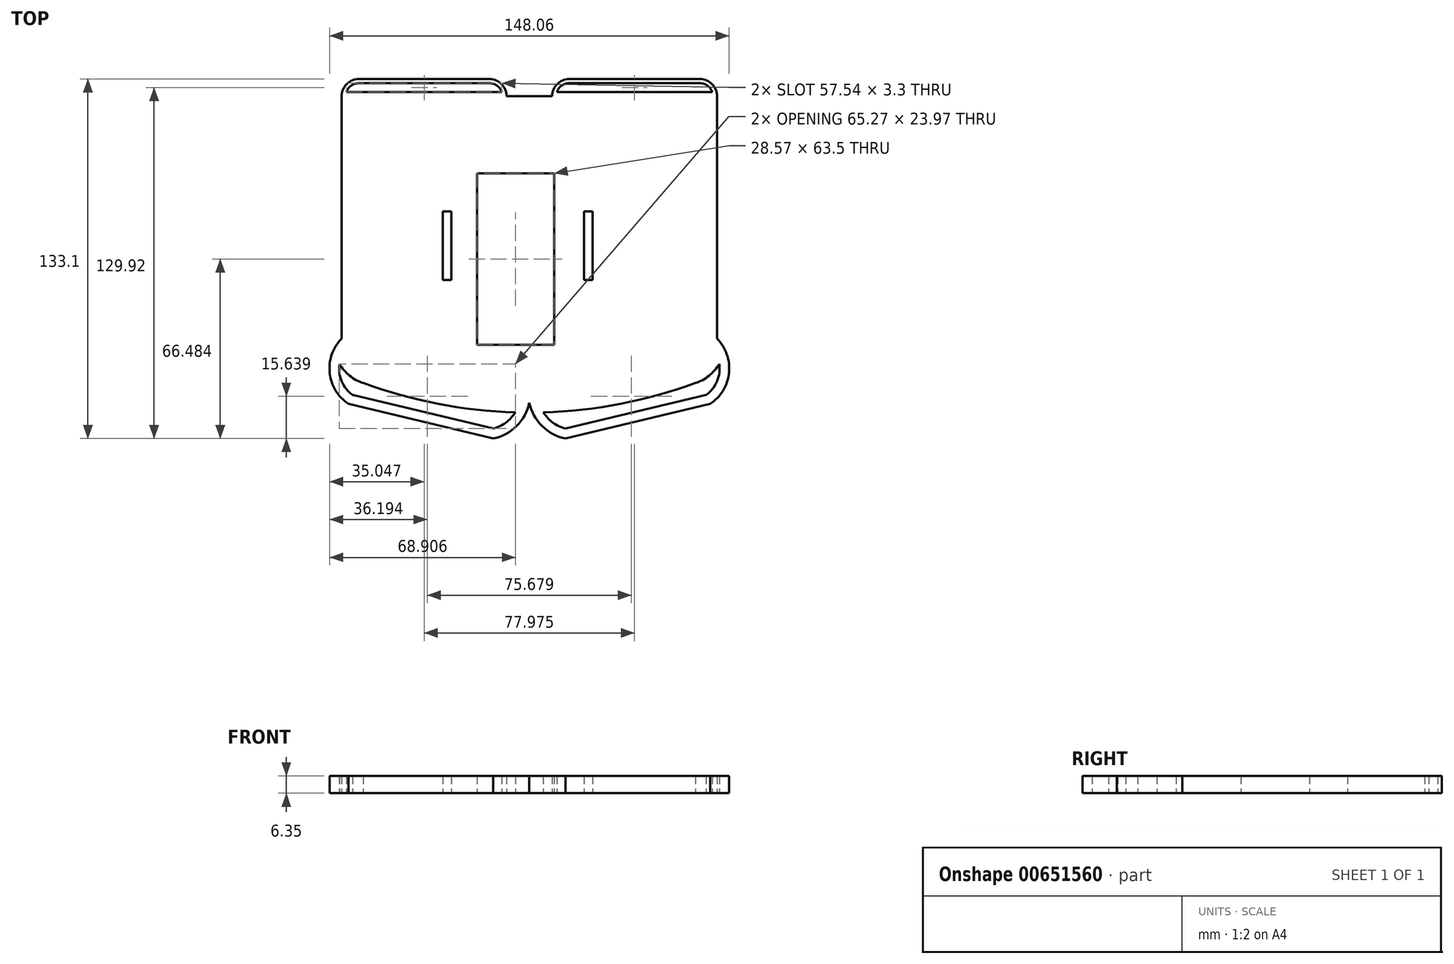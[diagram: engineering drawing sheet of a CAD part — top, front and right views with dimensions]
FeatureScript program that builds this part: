
annotation { "Feature Type Name" : "Feature", "Feature Type Description" : "" }
export const myFeature = defineFeature(function(context is Context, id is Id, definition is map)
    precondition{}
    {
        {
            var Q0;
            Q0=qCreatedBy(makeId("Top.planeOp"),FACE);
            var sketch = newSketch(context, id + "F0", { "sketchPlane" : qUnion([Q0])});
            skLineSegment(sketch, "E0", {"start": v(-4.1, 53.24) * mm, "end": v(12.8, 53.24) * mm});
            skPoint(sketch, "E1", {"position": v(4.35, -60.35) * mm});
            skLineSegment(sketch, "E2", {"start": v(-65.17, 41.8) * mm, "end": v(-65.17, -36.5) * mm});
            skLineSegment(sketch, "E3.MirrorCS", {"start": v(73.88, 41.8) * mm, "end": v(73.88, -36.5) * mm});
            skPoint(sketch, "E4.orphan", {"position": v(-65.17, -52.82) * mm});
            skPoint(sketch, "E5.orphan", {"position": v(73.88, -52.82) * mm});
            skPoint(sketch, "E6.visualSharp", {"position": v(-65.17, 53.24) * mm});
            skPoint(sketch, "E7.visualSharp", {"position": v(73.88, 53.24) * mm});
            skPoint(sketch, "E8.visualSharp", {"position": v(-65.17, -45.96) * mm});
            skPoint(sketch, "E9.visualSharp", {"position": v(73.88, -45.96) * mm});
            skLineSegment(sketch, "E10.top", {"start": v(-58.82, 59.59) * mm, "end": v(-10.44, 59.59) * mm});
            skLineSegment(sketch, "E10.left", {"start": v(-65.17, 41.8) * mm, "end": v(-65.17, 53.24) * mm});
            skLineSegment(sketch, "E11", {"start": v(-4.1, 53.24) * mm, "end": v(-4.1, 53.24) * mm});
            skPoint(sketch, "E12.orphan", {"position": v(4.35, 59.59) * mm});
            skPoint(sketch, "E13.visualSharp", {"position": v(-65.17, 59.59) * mm});
            skArc(sketch, "E13.filletArc", {"start": v(-58.82, 59.59) * mm, "mid": v(-63.31, 57.73) * mm, "end": v(-65.17, 53.24) * mm});
            skPoint(sketch, "E14.visualSharp", {"position": v(-4.1, 59.59) * mm});
            skArc(sketch, "E14.filletArc", {"start": v(-4.1, 53.24) * mm, "mid": v(-5.95, 57.73) * mm, "end": v(-10.44, 59.59) * mm});
            skArc(sketch, "E15.0", {"start": v(-58.82, 58.06) * mm, "mid": v(-61.65, 57.15) * mm, "end": v(-63.4, 54.76) * mm});
            skLineSegment(sketch, "E15.1", {"start": v(-58.82, 58.06) * mm, "end": v(-10.44, 58.06) * mm});
            skArc(sketch, "E15.2", {"start": v(-5.86, 54.76) * mm, "mid": v(-7.62, 57.15) * mm, "end": v(-10.44, 58.06) * mm});
            skLineSegment(sketch, "E15.3", {"start": v(-63.4, 54.76) * mm, "end": v(-5.86, 54.76) * mm});
            skArc(sketch, "E16.MirrorCS", {"start": v(12.8, 53.24) * mm, "mid": v(14.66, 57.73) * mm, "end": v(19.15, 59.59) * mm});
            skLineSegment(sketch, "E17.MirrorCS", {"start": v(67.53, 59.59) * mm, "end": v(19.15, 59.59) * mm});
            skArc(sketch, "E18.MirrorCS", {"start": v(14.57, 54.76) * mm, "mid": v(16.33, 57.15) * mm, "end": v(19.15, 58.06) * mm});
            skLineSegment(sketch, "E19.MirrorCS", {"start": v(67.53, 58.06) * mm, "end": v(19.15, 58.06) * mm});
            skLineSegment(sketch, "E20.MirrorCS", {"start": v(72.1, 54.76) * mm, "end": v(14.57, 54.76) * mm});
            skArc(sketch, "E21.MirrorCS", {"start": v(67.53, 59.59) * mm, "mid": v(72.02, 57.73) * mm, "end": v(73.88, 53.24) * mm});
            skArc(sketch, "E22.MirrorCS", {"start": v(67.53, 58.06) * mm, "mid": v(70.35, 57.15) * mm, "end": v(72.1, 54.76) * mm});
            skLineSegment(sketch, "E23", {"start": v(73.88, 41.8) * mm, "end": v(73.88, 53.24) * mm});
            skPoint(sketch, "E24.endSnap0", {"position": v(-62.66, -44.5) * mm});
            skLineSegment(sketch, "E25", {"start": v(-62.66, -60.72) * mm, "end": v(-8.99, -73.51) * mm});
            skArc(sketch, "E26", {"start": v(-65.17, -36.5) * mm, "mid": v(-69.6, -49.2) * mm, "end": v(-62.66, -60.72) * mm});
            skArc(sketch, "E27", {"start": v(-8.99, -73.51) * mm, "mid": v(-0.38, -68.9) * mm, "end": v(4.35, -60.35) * mm});
            skLineSegment(sketch, "E28.0", {"start": v(-66, -45.88) * mm, "end": v(-66, -45.88) * mm});
            skLineSegment(sketch, "E28.1", {"start": v(-61.17, -57.42) * mm, "end": v(-8.98, -69.86) * mm});
            skArc(sketch, "E28.2", {"start": v(-8.98, -69.86) * mm, "mid": v(-4.34, -67.62) * mm, "end": v(-0.85, -63.83) * mm});
            skArc(sketch, "E28.3", {"start": v(-66, -45.88) * mm, "mid": v(-65.16, -52.31) * mm, "end": v(-61.17, -57.42) * mm});
            skArc(sketch, "E28.4", {"start": v(-57.17, -52.98) * mm, "mid": v(-29.45, -60.68) * mm, "end": v(-0.85, -63.83) * mm});
            skArc(sketch, "E28.5", {"start": v(-66, -45.88) * mm, "mid": v(-62.25, -50.26) * mm, "end": v(-57.17, -52.98) * mm});
            skArc(sketch, "E29.MirrorCS", {"start": v(17.7, -73.51) * mm, "mid": v(9.09, -68.9) * mm, "end": v(4.35, -60.35) * mm});
            skArc(sketch, "E30.MirrorCS", {"start": v(17.7, -69.86) * mm, "mid": v(13.05, -67.62) * mm, "end": v(9.56, -63.83) * mm});
            skArc(sketch, "E31.MirrorCS", {"start": v(65.87, -52.98) * mm, "mid": v(38.15, -60.68) * mm, "end": v(9.56, -63.83) * mm});
            skLineSegment(sketch, "E32.MirrorCS", {"start": v(69.88, -57.42) * mm, "end": v(17.7, -69.86) * mm});
            skArc(sketch, "E33.MirrorCS", {"start": v(73.88, -36.5) * mm, "mid": v(78.3, -49.2) * mm, "end": v(71.37, -60.72) * mm});
            skArc(sketch, "E34.MirrorCS", {"start": v(74.71, -45.88) * mm, "mid": v(73.87, -52.31) * mm, "end": v(69.88, -57.42) * mm});
            skArc(sketch, "E35.MirrorCS", {"start": v(74.71, -45.88) * mm, "mid": v(70.96, -50.26) * mm, "end": v(65.87, -52.98) * mm});
            skLineSegment(sketch, "E36.MirrorCS", {"start": v(71.37, -60.72) * mm, "end": v(17.7, -73.51) * mm});
            skLineSegment(sketch, "E37.bottom", {"start": v(-15.06, 24.72) * mm, "end": v(13.51, 24.72) * mm});
            skLineSegment(sketch, "E37.top", {"start": v(-13.65, -38.78) * mm, "end": v(14.93, -38.78) * mm});
            skLineSegment(sketch, "E37.left", {"start": v(-15.06, 24.72) * mm, "end": v(-15.06, -38.78) * mm});
            skLineSegment(sketch, "E37.right", {"start": v(13.51, 24.72) * mm, "end": v(13.51, -38.78) * mm});
            skLineSegment(sketch, "E38.bottom", {"start": v(24.59, 10.58) * mm, "end": v(27.76, 10.58) * mm});
            skLineSegment(sketch, "E38.top", {"start": v(24.59, -14.82) * mm, "end": v(27.76, -14.82) * mm});
            skLineSegment(sketch, "E38.left", {"start": v(24.59, 10.58) * mm, "end": v(24.59, -14.82) * mm});
            skLineSegment(sketch, "E38.right", {"start": v(27.76, 10.58) * mm, "end": v(27.76, -14.82) * mm});
            skLineSegment(sketch, "E39.MirrorCS", {"start": v(-24.59, 10.58) * mm, "end": v(-24.59, -14.82) * mm});
            skLineSegment(sketch, "E40.MirrorCS", {"start": v(-24.59, 10.58) * mm, "end": v(-27.76, 10.58) * mm});
            skLineSegment(sketch, "E41.MirrorCS", {"start": v(-27.76, 10.58) * mm, "end": v(-27.76, -14.82) * mm});
            skLineSegment(sketch, "E42.MirrorCS", {"start": v(-24.59, -14.82) * mm, "end": v(-27.76, -14.82) * mm});
            skLineSegment(sketch, "E43", {"start": v(-13.65, -38.78) * mm, "end": v(-15.06, -38.78) * mm});
            skSolve(sketch);
        }
        {
            var Q0;
            Q0=makeQuery(id+"F0.imprint","IMPRINT",FACE,{"disambiguationData":[TD([[makeQuery(id+"F0.imprint","IMPRINT",EDGE,{"derivedFrom":sQuery(id+"F0.wireOp",EDGE,"E0")}),-1.0]])]});
            extrude(context, id + "F1", {"entities" : qUnion([Q0]), "depth" : 6.35 * mm, "offsetDistance" : 25.4 * mm});
        }
    });
